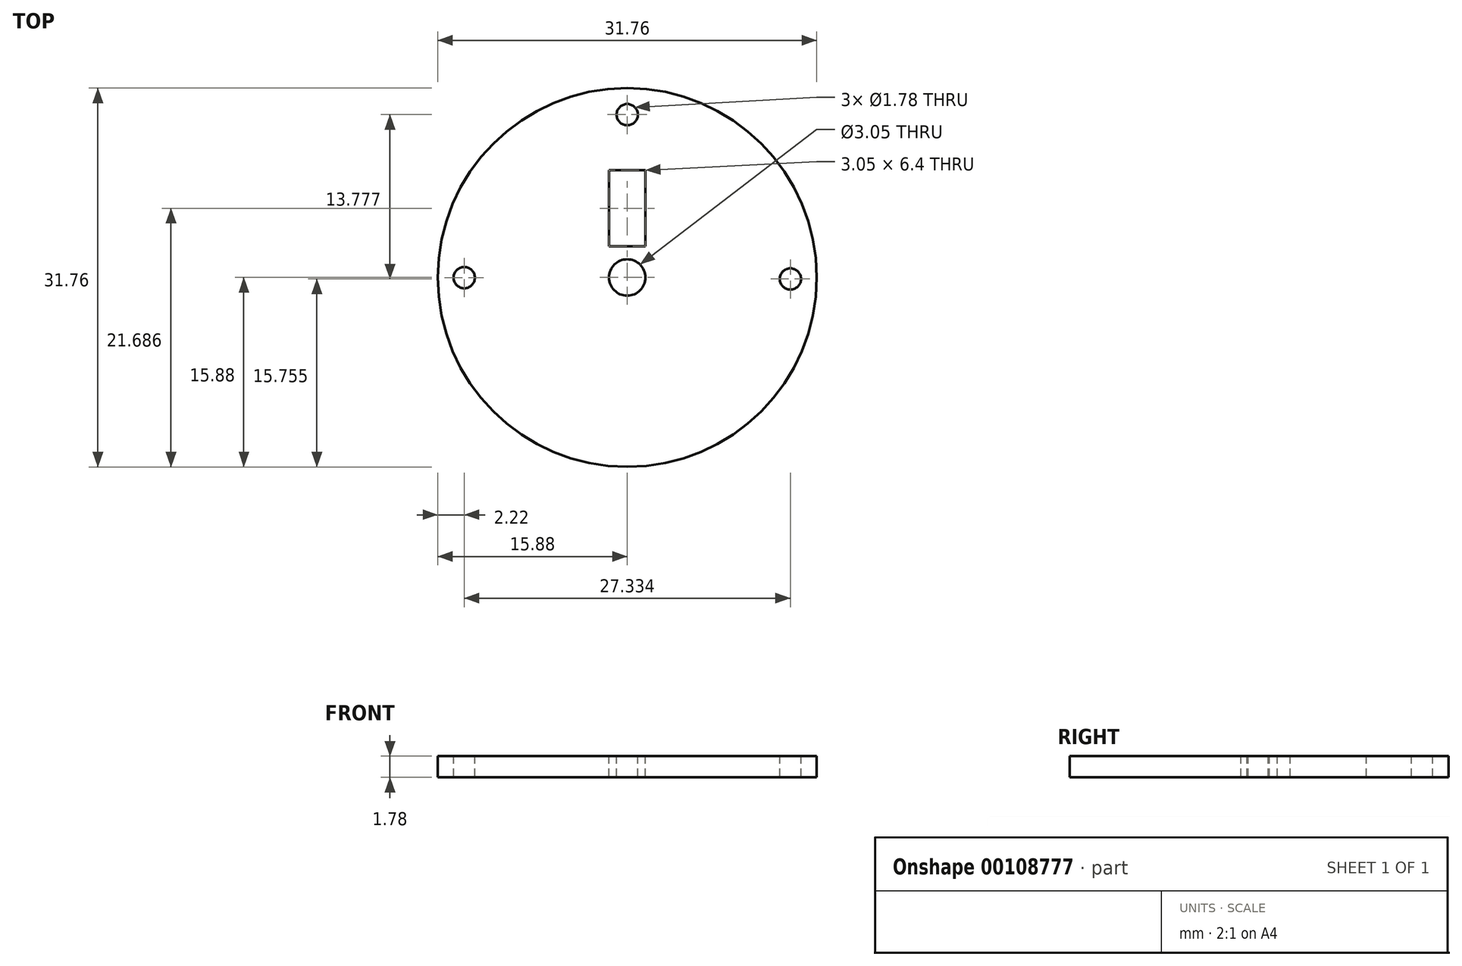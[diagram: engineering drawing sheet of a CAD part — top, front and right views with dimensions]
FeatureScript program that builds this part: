
annotation { "Feature Type Name" : "Feature", "Feature Type Description" : "" }
export const myFeature = defineFeature(function(context is Context, id is Id, definition is map)
    precondition{}
    {
        {
            var Q0;
            Q0=qCreatedBy(makeId("Top.planeOp"),FACE);
            var sketch = newSketch(context, id + "F0", { "sketchPlane" : qUnion([Q0])});
            skCircle(sketch, "E0", {"center": v(0, 0) * mm, "radius": 15.88 * mm});
            skSolve(sketch);
        }
        {
            var Q0;
            Q0=qSketchRegion(id+"F0",true);
            extrude(context, id + "F1", {"entities" : qUnion([Q0]), "oppositeDirection" : true, "depth" : 1.78 * mm});
        }
        {
            var Q0;
            Q0=makeQuery(id+"F1.opExtrude","CAP_FACE",FACE,{"disambiguationData":[OSD([sQuery(id+"F0.wireOp",EDGE,"E0")])],"isStart":true});
            var sketch = newSketch(context, id + "F2", { "sketchPlane" : qUnion([Q0])});
            skCircle(sketch, "E1", {"center": v(0, 0) * mm, "radius": 12.7 * mm});
            skSolve(sketch);
        }
        {
            var Q0;
            Q0=makeQuery(id+"F2.imprint","IMPRINT",FACE,{"disambiguationData":[TD([[makeQuery(id+"F2.imprint","IMPRINT",EDGE,{"derivedFrom":sQuery(id+"F2.wireOp",EDGE,"E1")}),-1.0]])]});
            var sketch = newSketch(context, id + "F3", { "sketchPlane" : qUnion([Q0])});
            skCircle(sketch, "E2", {"center": v(0, 13.65) * mm, "radius": 0.89 * mm});
            skCircle(sketch, "E3", {"center": v(-13.66, -0.02) * mm, "radius": 0.89 * mm});
            skCircle(sketch, "E4", {"center": v(13.67, -0.12) * mm, "radius": 0.89 * mm});
            skSolve(sketch);
        }
        {
            var Q0;
            Q0=qSketchRegion(id+"F3",true);
            extrude(context, id + "F4", {"entities" : qUnion([Q0]), "operationType" : NewBodyOperationType.REMOVE, "oppositeDirection" : true, "depth" : 1.91 * mm});
        }
        {
            var Q0;
            Q0=makeQuery(id+"F2.imprint","IMPRINT",FACE,{"disambiguationData":[TD([[makeQuery(id+"F2.imprint","IMPRINT",EDGE,{"derivedFrom":sQuery(id+"F2.wireOp",EDGE,"E1")}),-1.0]])]});
            var sketch = newSketch(context, id + "F5", { "sketchPlane" : qUnion([Q0])});
            skCircle(sketch, "E5", {"center": v(0, 0) * mm, "radius": 1.52 * mm});
            skLineSegment(sketch, "E6.bottom", {"start": v(1.52, 2.6) * mm, "end": v(-1.52, 2.6) * mm});
            skLineSegment(sketch, "E6.top", {"start": v(1.52, 9) * mm, "end": v(-1.52, 9) * mm});
            skLineSegment(sketch, "E6.left", {"start": v(1.52, 2.6) * mm, "end": v(1.52, 9) * mm});
            skLineSegment(sketch, "E6.right", {"start": v(-1.52, 2.6) * mm, "end": v(-1.52, 9) * mm});
            skPoint(sketch, "E6.middle", {"position": v(0, 5.8) * mm});
            skSolve(sketch);
        }
        {
            var Q0;
            Q0=qSketchRegion(id+"F5",true);
            extrude(context, id + "F6", {"entities" : qUnion([Q0]), "operationType" : NewBodyOperationType.REMOVE, "oppositeDirection" : true, "depth" : 2.22 * mm});
        }
    });
